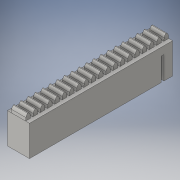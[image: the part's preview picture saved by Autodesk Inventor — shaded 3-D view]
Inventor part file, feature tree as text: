
AUTODESK INVENTOR PART (.ipt)
format: ipt  version: 2016 (Build 200138000, 138)  size: 388,608 bytes
history: native  units: in
note: dims shown in document units (in); Inventor stores cm internally (conversion verified against a paired STEP export)
features: extrude x8, sketch x8, projected_geometry x4
ambient origin geometry x8: Origin, YZ Plane, XZ Plane, XY Plane, X Axis, Y Axis, Z Axis, Center Point
bodies: Body1 (feature_tree)
feature tree (20):
  extrude  "Extrusion2"  Depth=2.5in
  sketch  "Sketch3"  dims[d6=0.385in d7=0.0in d9=0.092in]
  extrude  "Extrusion4"  Depth=0.385in
  extrude  "Extrusion6"  Depth=0.075in
  extrude  "Extrusion7"  Depth=0.05in
  extrude  "Extrusion8"  Depth=0.1in TaperAngle=0.0deg
  extrude  "Extrusion9"  Depth=0.385in TaperAngle=0.0deg
  extrude  "Extrusion10"  Depth=0.5814in
  extrude  "Extrusion11"  Depth=0.25in TaperAngle=0.0deg
  sketch  "Sketch2"  dims[d4=2.5in d5=0.435in]
  sketch  "Sketch4"  dims[d28=0.075in d29=0.075in]
  sketch  "Sketch5"  dims[d31=0.1in d32=0.05in]
  projected_geometry  "Projected Loop1"
  projected_geometry  "Projected Loop2"
  projected_geometry  "Projected Loop3"
  sketch  "Sketch6"  dims[d33=0.4in d34=0.0in d58=0.1in d59=0.0in]
  sketch  "Sketch7"  dims[d60=0.1in d61=0.385in d62=0.0in]
  sketch  "Sketch8"  dims[d63=0.5814in d64=0.5814in]
  sketch  "Sketch9"  dims[d72=7.874in d74=0.1271in d75=0.3937in d77=1.0in d79=0.25in d80=0.0in d81=0.05in d82=0.385in d83=0.0in d84=0.15in d85=0.05in d86=0.4in d87=0.385in d88=0.0in d89=0.385in d90=0.0in]
  projected_geometry  "Projected Loop4"
